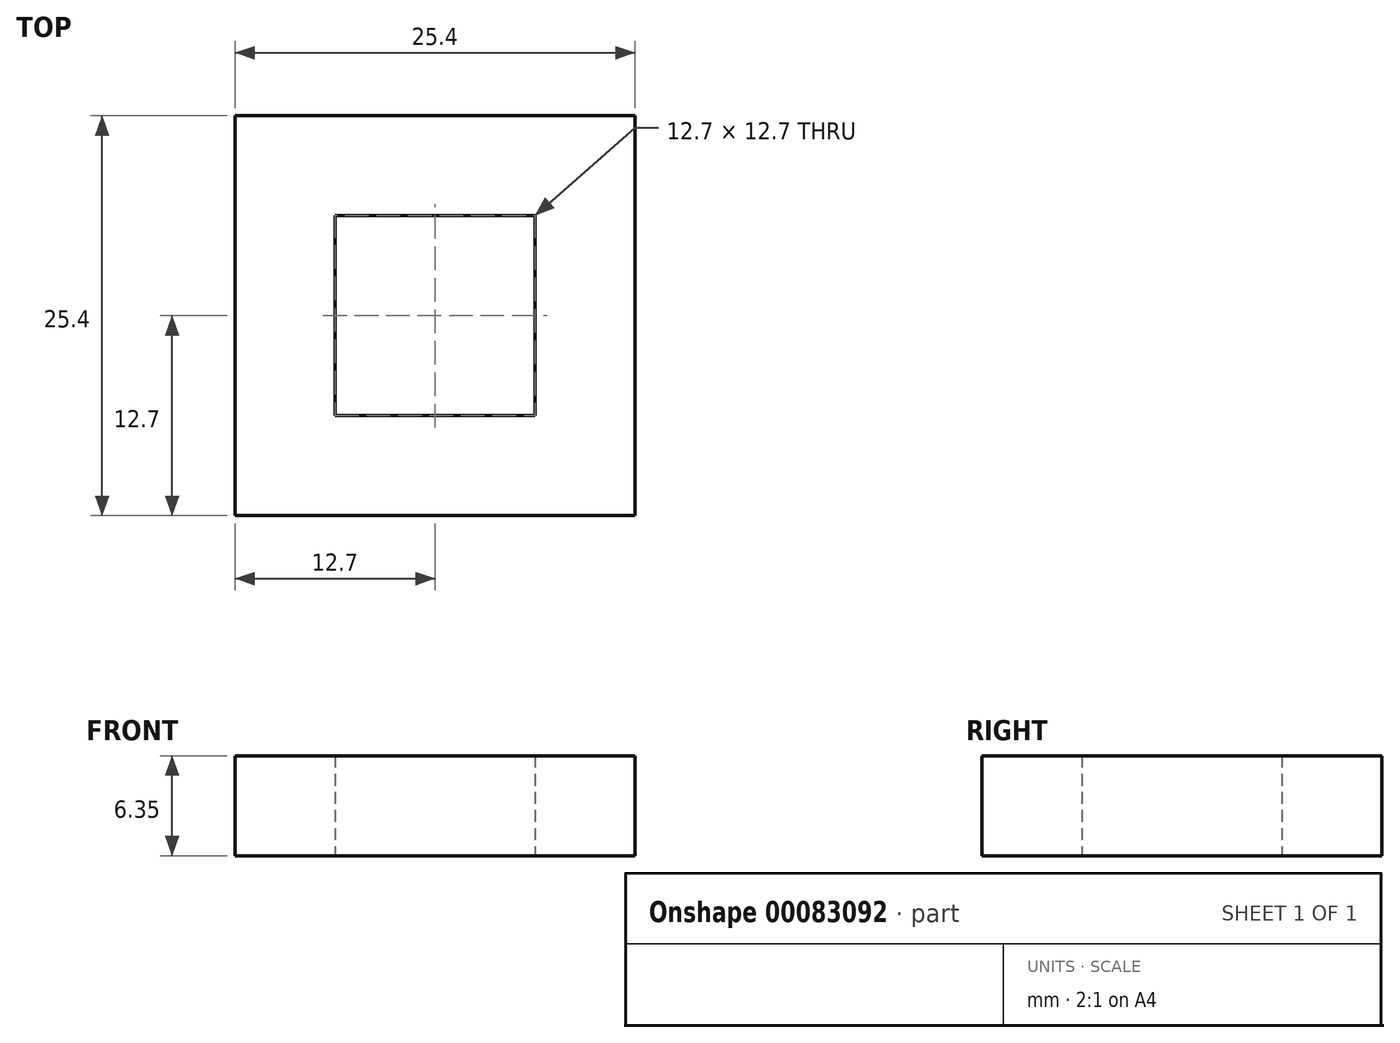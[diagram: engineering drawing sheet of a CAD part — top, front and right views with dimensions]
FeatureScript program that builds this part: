
annotation { "Feature Type Name" : "Feature", "Feature Type Description" : "" }
export const myFeature = defineFeature(function(context is Context, id is Id, definition is map)
    precondition{}
    {
        {
            var Q0;
            Q0=qCreatedBy(makeId("Top.planeOp"),FACE);
            var sketch = newSketch(context, id + "F0", { "sketchPlane" : qUnion([Q0])});
            skLineSegment(sketch, "E0.bottom", {"start": v(12.7, 12.7) * mm, "end": v(-12.7, 12.7) * mm});
            skLineSegment(sketch, "E0.top", {"start": v(12.7, -12.7) * mm, "end": v(-12.7, -12.7) * mm});
            skLineSegment(sketch, "E0.left", {"start": v(12.7, 12.7) * mm, "end": v(12.7, -12.7) * mm});
            skLineSegment(sketch, "E0.right", {"start": v(-12.7, 12.7) * mm, "end": v(-12.7, -12.7) * mm});
            skPoint(sketch, "E0.middle", {"position": v(0, 0) * mm});
            skLineSegment(sketch, "E1.0", {"start": v(6.35, 6.35) * mm, "end": v(-6.35, 6.35) * mm});
            skLineSegment(sketch, "E1.1", {"start": v(6.35, 6.35) * mm, "end": v(6.35, -6.35) * mm});
            skLineSegment(sketch, "E1.2", {"start": v(6.35, -6.35) * mm, "end": v(-6.35, -6.35) * mm});
            skLineSegment(sketch, "E1.3", {"start": v(-6.35, 6.35) * mm, "end": v(-6.35, -6.35) * mm});
            skSolve(sketch);
        }
        {
            var Q0;
            Q0 = qSketchRegion(id + "F0", true);
            extrude(context, id + "F1", {"entities" : qUnion([Q0]), "depth" : 6.35 * mm});
        }
    });
